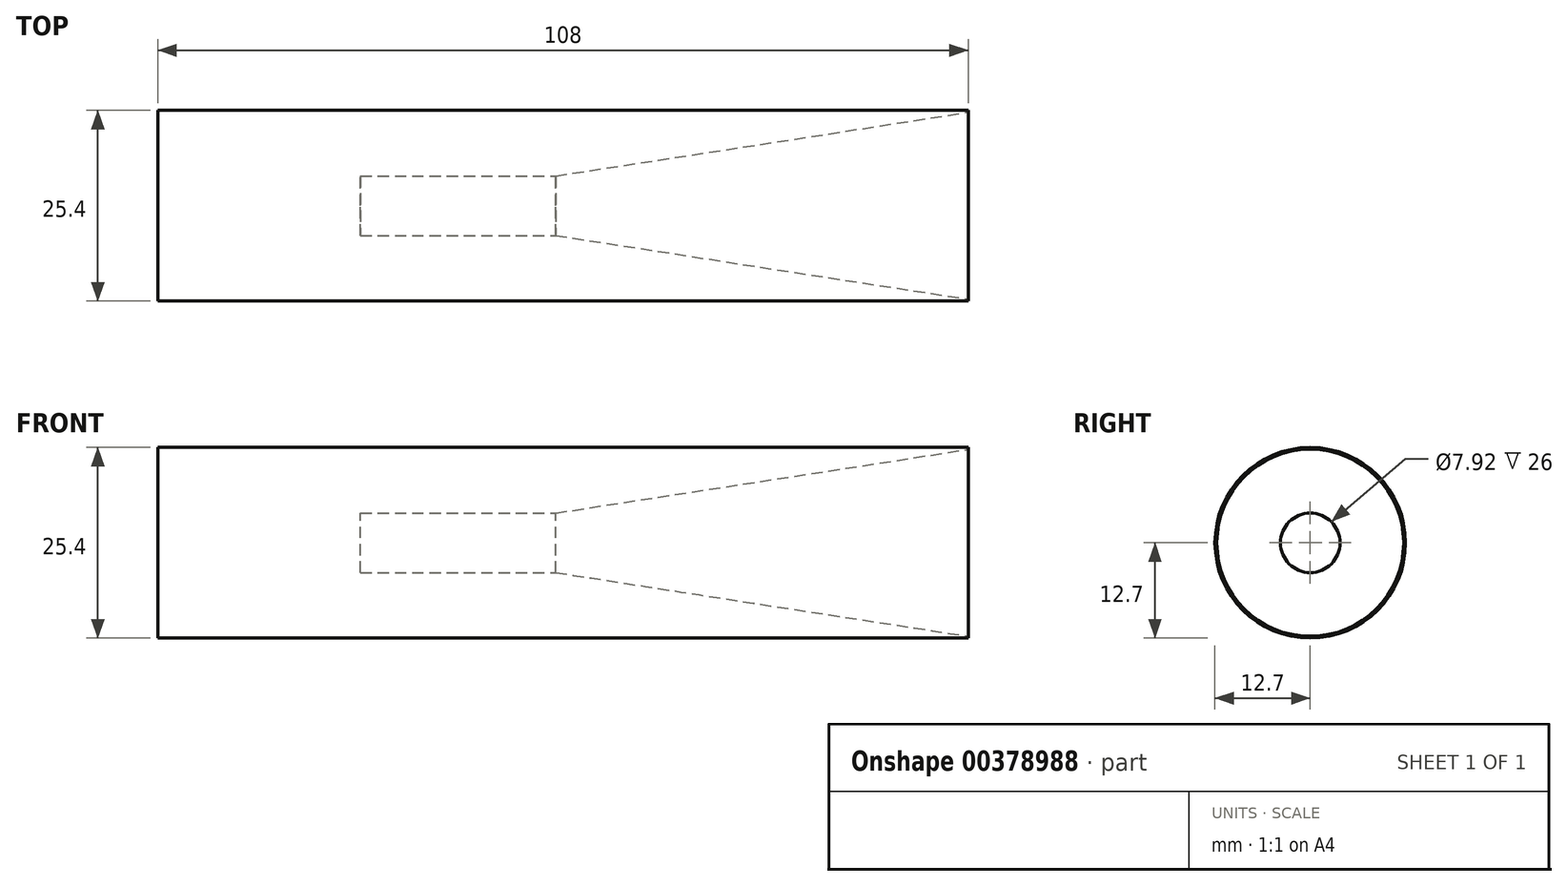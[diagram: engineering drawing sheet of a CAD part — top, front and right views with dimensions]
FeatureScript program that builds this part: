
annotation { "Feature Type Name" : "Feature", "Feature Type Description" : "" }
export const myFeature = defineFeature(function(context is Context, id is Id, definition is map)
    precondition{}
    {
        {
            var Q0;
            Q0=qCreatedBy(makeId("Front.planeOp"),FACE);
            var sketch = newSketch(context, id + "F0", { "sketchPlane" : qUnion([Q0])});
            skLineSegment(sketch, "E0", {"start": v(0, 0) * mm, "end": v(54, 0) * mm});
            skLineSegment(sketch, "E1", {"start": v(54, 0) * mm, "end": v(54, 12.45) * mm});
            skLineSegment(sketch, "E2", {"start": v(54, 12.45) * mm, "end": v(-1, 3.96) * mm});
            skLineSegment(sketch, "E3", {"start": v(-1, 3.96) * mm, "end": v(-27, 3.96) * mm});
            skLineSegment(sketch, "E4", {"start": v(-27, 3.96) * mm, "end": v(-27, 0) * mm});
            skLineSegment(sketch, "E5", {"start": v(-27, 0) * mm, "end": v(0, 0) * mm});
            skSolve(sketch);
        }
        {
            var Q0;
            Q0=qCreatedBy(makeId("Right.planeOp"),FACE);
            var sketch = newSketch(context, id + "F1", { "sketchPlane" : qUnion([Q0])});
            skCircle(sketch, "E6", {"center": v(0, 0) * mm, "radius": 12.7 * mm});
            skSolve(sketch);
        }
        {
            var Q0;
            Q0 = qSketchRegion(id + "F1", true);
            extrude(context, id + "F2", {"entities" : qUnion([Q0]), "endBound" : BoundingType.SYMMETRIC, "depth" : 108 * mm});
        }
        {
            var Q0;
            Q0 = qSketchRegion(id + "F0", true);
            var Q1;
            Q1=sQuery(id+"F0.wireOp",EDGE,"E5");
            revolve(context, id + "F3", {"operationType" : NewBodyOperationType.REMOVE, "entities" : qUnion([Q0]), "axis" : qUnion([Q1]), "revolveType" : RevolveType.FULL, "oppositeDirection" : true});
        }
    });
